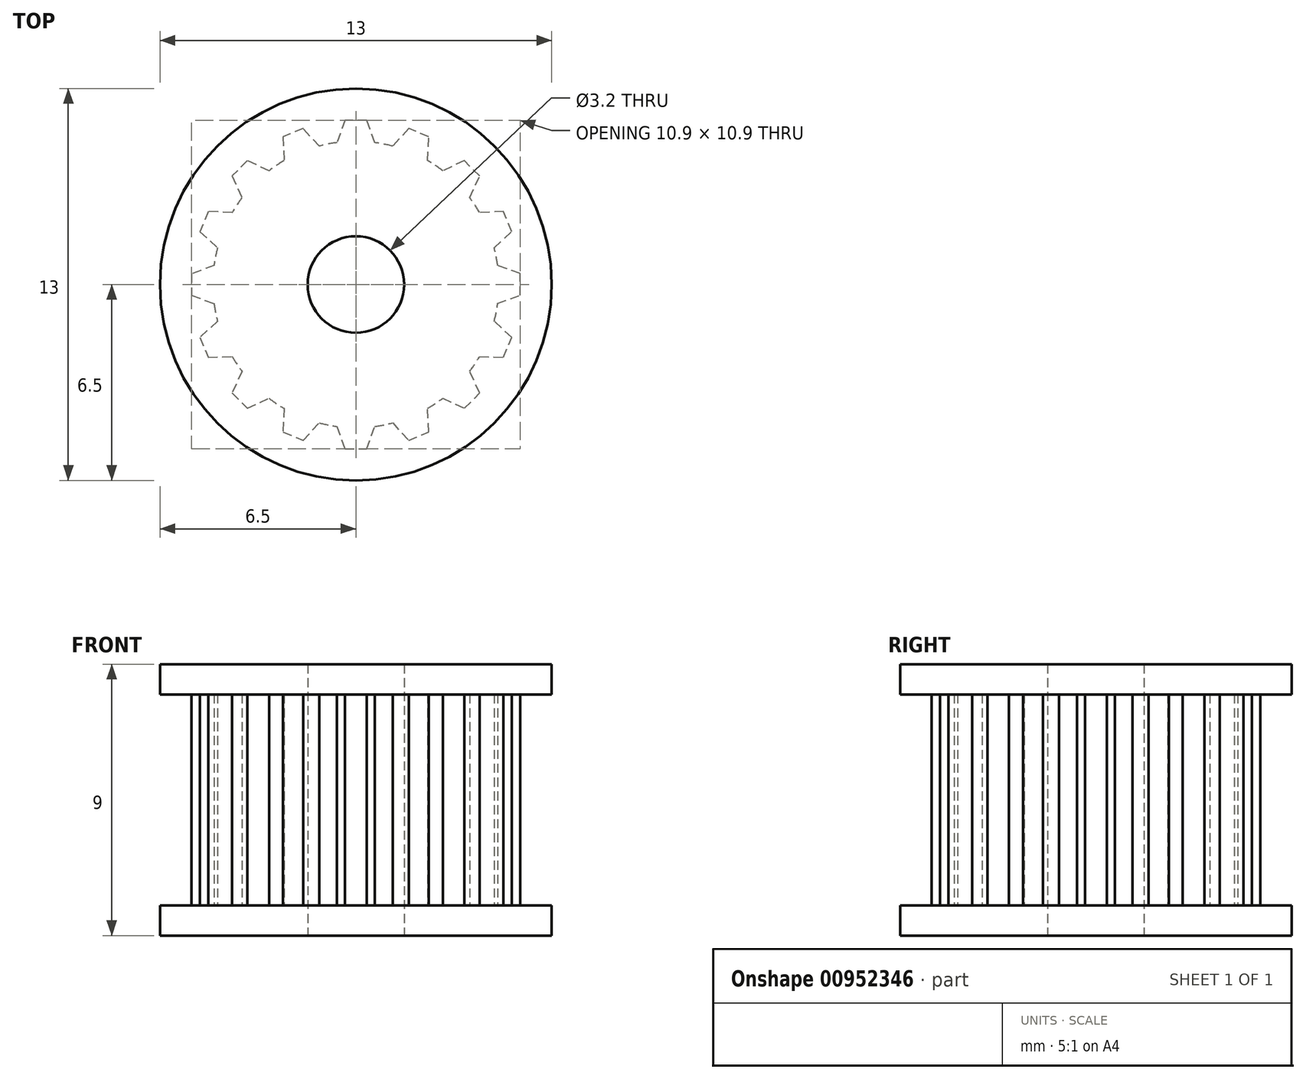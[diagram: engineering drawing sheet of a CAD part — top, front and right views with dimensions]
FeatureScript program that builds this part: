
annotation { "Feature Type Name" : "Feature", "Feature Type Description" : "" }
export const myFeature = defineFeature(function(context is Context, id is Id, definition is map)
    precondition{}
    {
        {
            var Q0;
            Q0=qCreatedBy(makeId("Top.planeOp"),FACE);
            var sketch = newSketch(context, id + "F0", { "sketchPlane" : qUnion([Q0])});
            skCircle(sketch, "E0", {"center": v(0, 0) * mm, "radius": 1.6 * mm});
            skCircle(sketch, "E1", {"center": v(0, 0) * mm, "radius": 4.75 * mm});
            skCircle(sketch, "E2", {"center": v(0, 0) * mm, "radius": 6.5 * mm});
            skLineSegment(sketch, "E3", {"start": v(-0.75, 4.38) * mm, "end": v(0.75, 4.38) * mm});
            skLineSegment(sketch, "E4", {"start": v(0.75, 4.38) * mm, "end": v(0.36, 5.45) * mm});
            skLineSegment(sketch, "E5", {"start": v(0.36, 5.45) * mm, "end": v(-0.36, 5.45) * mm});
            skLineSegment(sketch, "E6", {"start": v(-0.36, 5.45) * mm, "end": v(-0.75, 4.38) * mm});
            skLineSegment(sketch, "E7", {"start": v(-1.44, 4.75) * mm, "end": v(0.88, 4.75) * mm, "construction": true});
            skPoint(sketch, "E8", {"position": v(0, 4.38) * mm});
            skLineSegment(sketch, "E9", {"start": v(0, -2.38) * mm, "end": v(0, 7.47) * mm, "construction": true});
            skSolve(sketch);
        }
        {
            var Q0;
            Q0=makeQuery(id+"F0.imprint","IMPRINT",FACE,{"disambiguationData":[TD([[makeQuery(id+"F0.imprint","IMPRINT",EDGE,{"derivedFrom":sQuery(id+"F0.wireOp",EDGE,"E0")}),-1.0]])]});
            var Q1;
            {var subQ5=sQuery(id+"F0.wireOp",EDGE,"E5");Q1=makeQuery(id+"F0.imprint","IMPRINT",FACE,{"disambiguationData":[TD([[makeQuery(id+"F0.imprint","IMPRINT",EDGE,{"derivedFrom":subQ5}),1.0]])]});}
            var Q2;
            {var subQ5=sQuery(id+"F0.wireOp",EDGE,"E3");Q2=makeQuery(id+"F0.imprint","IMPRINT",FACE,{"disambiguationData":[TD([[makeQuery(id+"F0.imprint","IMPRINT",EDGE,{"derivedFrom":subQ5}),1.0]])]});}
            extrude(context, id + "F1", {"entities" : qUnion([Q0, Q1, Q2]), "endBound" : BoundingType.SYMMETRIC, "depth" : 7 * mm, "offsetDistance" : 25 * mm});
        }
        {
            var Q0;
            Q0=qCreatedBy(makeId("Front.planeOp"),FACE);
            var sketch = newSketch(context, id + "F2", { "sketchPlane" : qUnion([Q0])});
            skLineSegment(sketch, "E10", {"start": v(0, 5.96) * mm, "end": v(0, -5.73) * mm});
            skSolve(sketch);
        }
        {
            var Q0;
            Q0=makeQuery(id+"F1.opExtrude","SWEPT_BODY",BODY,{"disambiguationData":[OSD([sQuery(id+"F0.wireOp",EDGE,"E1"),sQuery(id+"F0.wireOp",EDGE,"CzVH5QZO-12Nw-GHuI-hNxM-fU3eulkCBIGX.bottom"),sQuery(id+"F0.wireOp",EDGE,"CzVH5QZO-12Nw-GHuI-hNxM-fU3eulkCBIGX.left"),sQuery(id+"F0.wireOp",EDGE,"CzVH5QZO-12Nw-GHuI-hNxM-fU3eulkCBIGX.right")])]});
            var Q1;
            Q1=sQuery(id+"F2.wireOp",EDGE,"E10");
            circularPattern(context, id + "F3", {"entities" : qUnion([Q0]), "axis" : qUnion([Q1]), "angle" : 360 * degree, "instanceCount" : 16, "equalSpace" : true});
        }
        {
            var Q0;
            Q0=makeQuery(id+"F3.opPattern","COPY",BODY,{"derivedFrom":makeQuery(id+"F1.opExtrude","SWEPT_BODY",BODY,{"disambiguationData":[OSD([sQuery(id+"F0.wireOp",EDGE,"E0"),sQuery(id+"F0.wireOp",EDGE,"E1"),sQuery(id+"F0.wireOp",EDGE,"E4"),sQuery(id+"F0.wireOp",EDGE,"E5"),sQuery(id+"F0.wireOp",EDGE,"E6")])]}),"instanceName":"1"});
            var Q1;
            Q1=makeQuery(id+"F3.opPattern","COPY",BODY,{"derivedFrom":makeQuery(id+"F1.opExtrude","SWEPT_BODY",BODY,{"disambiguationData":[OSD([sQuery(id+"F0.wireOp",EDGE,"E0"),sQuery(id+"F0.wireOp",EDGE,"E1"),sQuery(id+"F0.wireOp",EDGE,"E4"),sQuery(id+"F0.wireOp",EDGE,"E5"),sQuery(id+"F0.wireOp",EDGE,"E6")])]}),"instanceName":"2"});
            var Q2;
            Q2=makeQuery(id+"F3.opPattern","COPY",BODY,{"derivedFrom":makeQuery(id+"F1.opExtrude","SWEPT_BODY",BODY,{"disambiguationData":[OSD([sQuery(id+"F0.wireOp",EDGE,"E0"),sQuery(id+"F0.wireOp",EDGE,"E1"),sQuery(id+"F0.wireOp",EDGE,"E4"),sQuery(id+"F0.wireOp",EDGE,"E5"),sQuery(id+"F0.wireOp",EDGE,"E6")])]}),"instanceName":"3"});
            var Q3;
            Q3=makeQuery(id+"F3.opPattern","COPY",BODY,{"derivedFrom":makeQuery(id+"F1.opExtrude","SWEPT_BODY",BODY,{"disambiguationData":[OSD([sQuery(id+"F0.wireOp",EDGE,"E0"),sQuery(id+"F0.wireOp",EDGE,"E1"),sQuery(id+"F0.wireOp",EDGE,"E4"),sQuery(id+"F0.wireOp",EDGE,"E5"),sQuery(id+"F0.wireOp",EDGE,"E6")])]}),"instanceName":"4"});
            var Q4;
            Q4=makeQuery(id+"F3.opPattern","COPY",BODY,{"derivedFrom":makeQuery(id+"F1.opExtrude","SWEPT_BODY",BODY,{"disambiguationData":[OSD([sQuery(id+"F0.wireOp",EDGE,"E0"),sQuery(id+"F0.wireOp",EDGE,"E1"),sQuery(id+"F0.wireOp",EDGE,"E4"),sQuery(id+"F0.wireOp",EDGE,"E5"),sQuery(id+"F0.wireOp",EDGE,"E6")])]}),"instanceName":"5"});
            var Q5;
            Q5=makeQuery(id+"F3.opPattern","COPY",BODY,{"derivedFrom":makeQuery(id+"F1.opExtrude","SWEPT_BODY",BODY,{"disambiguationData":[OSD([sQuery(id+"F0.wireOp",EDGE,"E0"),sQuery(id+"F0.wireOp",EDGE,"E1"),sQuery(id+"F0.wireOp",EDGE,"E4"),sQuery(id+"F0.wireOp",EDGE,"E5"),sQuery(id+"F0.wireOp",EDGE,"E6")])]}),"instanceName":"7"});
            var Q6;
            Q6=makeQuery(id+"F3.opPattern","COPY",BODY,{"derivedFrom":makeQuery(id+"F1.opExtrude","SWEPT_BODY",BODY,{"disambiguationData":[OSD([sQuery(id+"F0.wireOp",EDGE,"E0"),sQuery(id+"F0.wireOp",EDGE,"E1"),sQuery(id+"F0.wireOp",EDGE,"E4"),sQuery(id+"F0.wireOp",EDGE,"E5"),sQuery(id+"F0.wireOp",EDGE,"E6")])]}),"instanceName":"9"});
            var Q7;
            Q7=makeQuery(id+"F3.opPattern","COPY",BODY,{"derivedFrom":makeQuery(id+"F1.opExtrude","SWEPT_BODY",BODY,{"disambiguationData":[OSD([sQuery(id+"F0.wireOp",EDGE,"E0"),sQuery(id+"F0.wireOp",EDGE,"E1"),sQuery(id+"F0.wireOp",EDGE,"E4"),sQuery(id+"F0.wireOp",EDGE,"E5"),sQuery(id+"F0.wireOp",EDGE,"E6")])]}),"instanceName":"10"});
            var Q8;
            Q8=makeQuery(id+"F3.opPattern","COPY",BODY,{"derivedFrom":makeQuery(id+"F1.opExtrude","SWEPT_BODY",BODY,{"disambiguationData":[OSD([sQuery(id+"F0.wireOp",EDGE,"E0"),sQuery(id+"F0.wireOp",EDGE,"E1"),sQuery(id+"F0.wireOp",EDGE,"E4"),sQuery(id+"F0.wireOp",EDGE,"E5"),sQuery(id+"F0.wireOp",EDGE,"E6")])]}),"instanceName":"8"});
            var Q9;
            Q9=makeQuery(id+"F3.opPattern","COPY",BODY,{"derivedFrom":makeQuery(id+"F1.opExtrude","SWEPT_BODY",BODY,{"disambiguationData":[OSD([sQuery(id+"F0.wireOp",EDGE,"E0"),sQuery(id+"F0.wireOp",EDGE,"E1"),sQuery(id+"F0.wireOp",EDGE,"E4"),sQuery(id+"F0.wireOp",EDGE,"E5"),sQuery(id+"F0.wireOp",EDGE,"E6")])]}),"instanceName":"6"});
            var Q10;
            Q10=makeQuery(id+"F3.opPattern","COPY",BODY,{"derivedFrom":makeQuery(id+"F1.opExtrude","SWEPT_BODY",BODY,{"disambiguationData":[OSD([sQuery(id+"F0.wireOp",EDGE,"E0"),sQuery(id+"F0.wireOp",EDGE,"E1"),sQuery(id+"F0.wireOp",EDGE,"E4"),sQuery(id+"F0.wireOp",EDGE,"E5"),sQuery(id+"F0.wireOp",EDGE,"E6")])]}),"instanceName":"11"});
            var Q11;
            Q11=makeQuery(id+"F3.opPattern","COPY",BODY,{"derivedFrom":makeQuery(id+"F1.opExtrude","SWEPT_BODY",BODY,{"disambiguationData":[OSD([sQuery(id+"F0.wireOp",EDGE,"E0"),sQuery(id+"F0.wireOp",EDGE,"E1"),sQuery(id+"F0.wireOp",EDGE,"E4"),sQuery(id+"F0.wireOp",EDGE,"E5"),sQuery(id+"F0.wireOp",EDGE,"E6")])]}),"instanceName":"12"});
            var Q12;
            Q12=makeQuery(id+"F3.opPattern","COPY",BODY,{"derivedFrom":makeQuery(id+"F1.opExtrude","SWEPT_BODY",BODY,{"disambiguationData":[OSD([sQuery(id+"F0.wireOp",EDGE,"E0"),sQuery(id+"F0.wireOp",EDGE,"E1"),sQuery(id+"F0.wireOp",EDGE,"E4"),sQuery(id+"F0.wireOp",EDGE,"E5"),sQuery(id+"F0.wireOp",EDGE,"E6")])]}),"instanceName":"14"});
            var Q13;
            Q13=makeQuery(id+"F1.opExtrude","SWEPT_BODY",BODY,{"disambiguationData":[OSD([sQuery(id+"F0.wireOp",EDGE,"E0"),sQuery(id+"F0.wireOp",EDGE,"E1"),sQuery(id+"F0.wireOp",EDGE,"E4"),sQuery(id+"F0.wireOp",EDGE,"E5"),sQuery(id+"F0.wireOp",EDGE,"E6")])]});
            var Q14;
            Q14=makeQuery(id+"F3.opPattern","COPY",BODY,{"derivedFrom":makeQuery(id+"F1.opExtrude","SWEPT_BODY",BODY,{"disambiguationData":[OSD([sQuery(id+"F0.wireOp",EDGE,"E0"),sQuery(id+"F0.wireOp",EDGE,"E1"),sQuery(id+"F0.wireOp",EDGE,"E4"),sQuery(id+"F0.wireOp",EDGE,"E5"),sQuery(id+"F0.wireOp",EDGE,"E6")])]}),"instanceName":"13"});
            var Q15;
            Q15=makeQuery(id+"F3.opPattern","COPY",BODY,{"derivedFrom":makeQuery(id+"F1.opExtrude","SWEPT_BODY",BODY,{"disambiguationData":[OSD([sQuery(id+"F0.wireOp",EDGE,"E0"),sQuery(id+"F0.wireOp",EDGE,"E1"),sQuery(id+"F0.wireOp",EDGE,"E4"),sQuery(id+"F0.wireOp",EDGE,"E5"),sQuery(id+"F0.wireOp",EDGE,"E6")])]}),"instanceName":"15"});
            booleanBodies(context, id + "F4", {"operationType" : BooleanOperationType.UNION, "tools" : qUnion([Q0, Q1, Q2, Q3, Q4, Q5, Q6, Q7, Q8, Q9, Q10, Q11, Q12, Q13, Q14, Q15])});
        }
        {
            var Q0;
            {var subQ0=makeQuery(id+"F1.opExtrude","CAP_FACE",FACE,{"disambiguationData":[OSD([sQuery(id+"F0.wireOp",EDGE,"E0"),sQuery(id+"F0.wireOp",EDGE,"E1"),sQuery(id+"F0.wireOp",EDGE,"E4"),sQuery(id+"F0.wireOp",EDGE,"E5"),sQuery(id+"F0.wireOp",EDGE,"E6")])],"isStart":false});Q0=makeQuery(id+"F4.opBoolean","MERGE",FACE,{"derivedFrom":[subQ0,makeQuery(id+"F3.opPattern","COPY",FACE,{"derivedFrom":subQ0,"instanceName":"1"}),makeQuery(id+"F3.opPattern","COPY",FACE,{"derivedFrom":subQ0,"instanceName":"2"}),makeQuery(id+"F3.opPattern","COPY",FACE,{"derivedFrom":subQ0,"instanceName":"3"}),makeQuery(id+"F3.opPattern","COPY",FACE,{"derivedFrom":subQ0,"instanceName":"4"}),makeQuery(id+"F3.opPattern","COPY",FACE,{"derivedFrom":subQ0,"instanceName":"5"}),makeQuery(id+"F3.opPattern","COPY",FACE,{"derivedFrom":subQ0,"instanceName":"6"}),makeQuery(id+"F3.opPattern","COPY",FACE,{"derivedFrom":subQ0,"instanceName":"7"}),makeQuery(id+"F3.opPattern","COPY",FACE,{"derivedFrom":subQ0,"instanceName":"8"}),makeQuery(id+"F3.opPattern","COPY",FACE,{"derivedFrom":subQ0,"instanceName":"9"}),makeQuery(id+"F3.opPattern","COPY",FACE,{"derivedFrom":subQ0,"instanceName":"10"}),makeQuery(id+"F3.opPattern","COPY",FACE,{"derivedFrom":subQ0,"instanceName":"11"}),makeQuery(id+"F3.opPattern","COPY",FACE,{"derivedFrom":subQ0,"instanceName":"12"}),makeQuery(id+"F3.opPattern","COPY",FACE,{"derivedFrom":subQ0,"instanceName":"13"}),makeQuery(id+"F3.opPattern","COPY",FACE,{"derivedFrom":subQ0,"instanceName":"14"}),makeQuery(id+"F3.opPattern","COPY",FACE,{"derivedFrom":subQ0,"instanceName":"15"})]});}
            var sketch = newSketch(context, id + "F5", { "sketchPlane" : qUnion([Q0])});
            skCircle(sketch, "E11.0", {"center": v(0, 0) * mm, "radius": 6.5 * mm});
            skSolve(sketch);
        }
        {
            var Q0;
            Q0 = qSketchRegion(id + "F5", true);
            var Q1;
            Q1=sQuery(id+"FeYlwFavrc0MB7O_1.wireOp",EDGE,"eb92d3ff-e652-4a5a-b473-ca1a323c532c.2");
            extrude(context, id + "F6", {"entities" : qUnion([Q0]), "operationType" : NewBodyOperationType.ADD, "surfaceEntities" : qUnion([Q1]), "depth" : 1 * mm, "offsetDistance" : 25 * mm});
        }
        {
            var Q0;
            {var subQ0=makeQuery(id+"F1.opExtrude","CAP_FACE",FACE,{"disambiguationData":[OSD([sQuery(id+"F0.wireOp",EDGE,"E0"),sQuery(id+"F0.wireOp",EDGE,"E1"),sQuery(id+"F0.wireOp",EDGE,"E4"),sQuery(id+"F0.wireOp",EDGE,"E5"),sQuery(id+"F0.wireOp",EDGE,"E6")])],"isStart":true});Q0=makeQuery(id+"F4.opBoolean","MERGE",FACE,{"derivedFrom":[subQ0,makeQuery(id+"F3.opPattern","COPY",FACE,{"derivedFrom":subQ0,"instanceName":"1"}),makeQuery(id+"F3.opPattern","COPY",FACE,{"derivedFrom":subQ0,"instanceName":"2"}),makeQuery(id+"F3.opPattern","COPY",FACE,{"derivedFrom":subQ0,"instanceName":"3"}),makeQuery(id+"F3.opPattern","COPY",FACE,{"derivedFrom":subQ0,"instanceName":"4"}),makeQuery(id+"F3.opPattern","COPY",FACE,{"derivedFrom":subQ0,"instanceName":"5"}),makeQuery(id+"F3.opPattern","COPY",FACE,{"derivedFrom":subQ0,"instanceName":"6"}),makeQuery(id+"F3.opPattern","COPY",FACE,{"derivedFrom":subQ0,"instanceName":"7"}),makeQuery(id+"F3.opPattern","COPY",FACE,{"derivedFrom":subQ0,"instanceName":"8"}),makeQuery(id+"F3.opPattern","COPY",FACE,{"derivedFrom":subQ0,"instanceName":"9"}),makeQuery(id+"F3.opPattern","COPY",FACE,{"derivedFrom":subQ0,"instanceName":"10"}),makeQuery(id+"F3.opPattern","COPY",FACE,{"derivedFrom":subQ0,"instanceName":"11"}),makeQuery(id+"F3.opPattern","COPY",FACE,{"derivedFrom":subQ0,"instanceName":"12"}),makeQuery(id+"F3.opPattern","COPY",FACE,{"derivedFrom":subQ0,"instanceName":"13"}),makeQuery(id+"F3.opPattern","COPY",FACE,{"derivedFrom":subQ0,"instanceName":"14"}),makeQuery(id+"F3.opPattern","COPY",FACE,{"derivedFrom":subQ0,"instanceName":"15"})]});}
            var sketch = newSketch(context, id + "F7", { "sketchPlane" : qUnion([Q0])});
            skCircle(sketch, "E12.0", {"center": v(0, 0) * mm, "radius": 6.5 * mm});
            skSolve(sketch);
        }
        {
            var Q0;
            Q0 = qSketchRegion(id + "F7", true);
            extrude(context, id + "F8", {"entities" : qUnion([Q0]), "operationType" : NewBodyOperationType.ADD, "depth" : 1 * mm, "offsetDistance" : 25 * mm});
        }
        {
            var Q0;
            Q0=makeQuery(id+"F0.imprint","IMPRINT",FACE,{"disambiguationData":[TD([[makeQuery(id+"F0.imprint","IMPRINT",EDGE,{"derivedFrom":sQuery(id+"F0.wireOp",EDGE,"E0")}),1.0]])]});
            extrude(context, id + "F9", {"entities" : qUnion([Q0]), "operationType" : NewBodyOperationType.REMOVE, "endBound" : BoundingType.SYMMETRIC, "oppositeDirection" : true, "depth" : 25 * mm, "offsetDistance" : 25 * mm});
        }
    });
